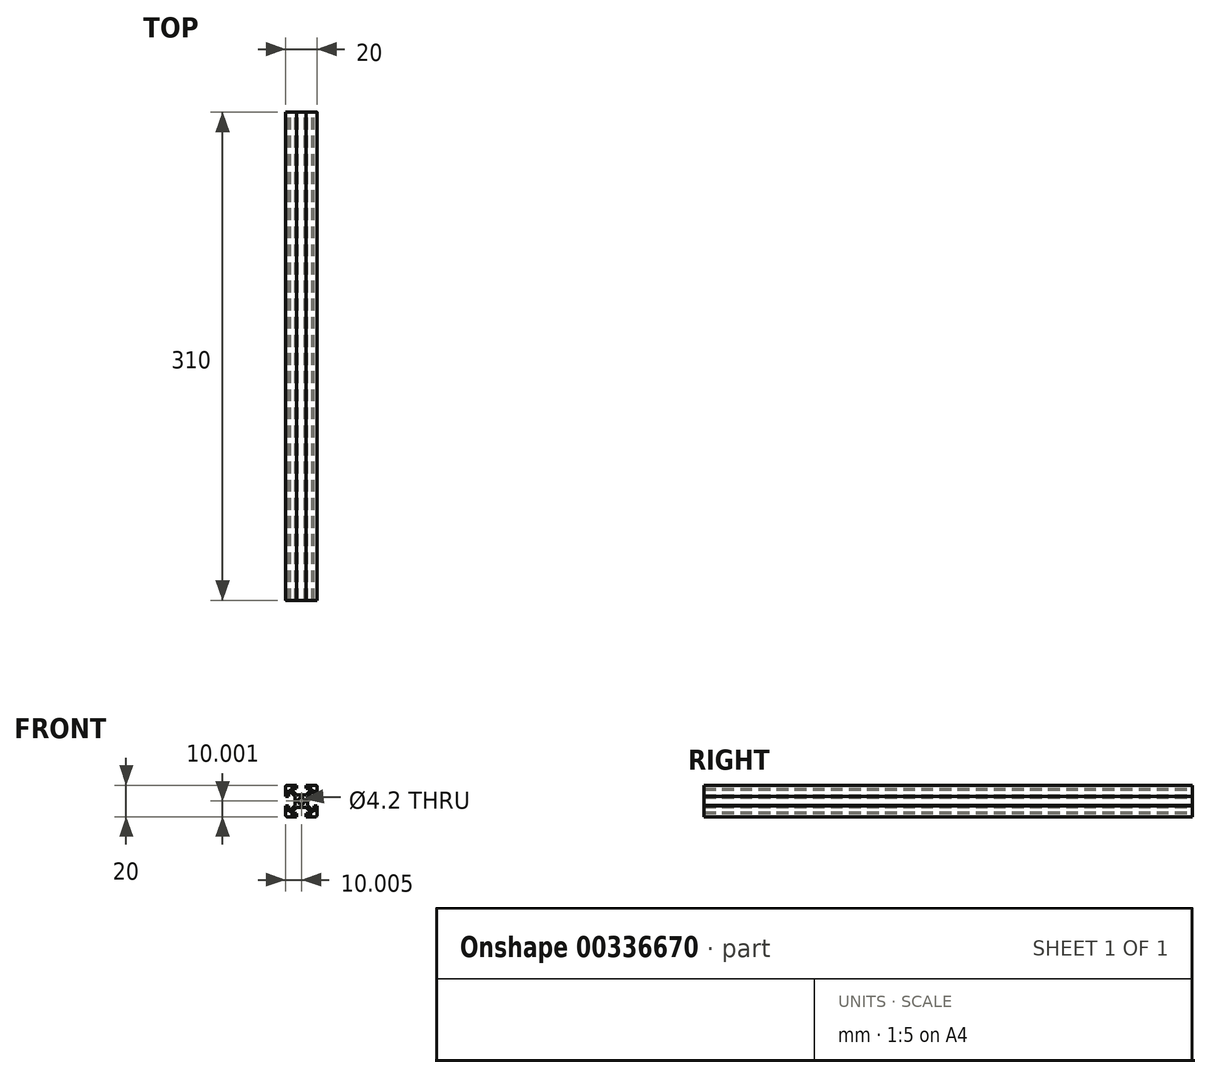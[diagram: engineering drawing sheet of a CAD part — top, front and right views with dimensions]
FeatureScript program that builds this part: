
annotation { "Feature Type Name" : "Feature", "Feature Type Description" : "" }
export const myFeature = defineFeature(function(context is Context, id is Id, definition is map)
    precondition{}
    {
        {
            var Q0;
            Q0=qCreatedBy(makeId("Front.planeOp"),FACE);
            var sketch = newSketch(context, id + "F0", { "sketchPlane" : qUnion([Q0])});
            skCircle(sketch, "E0", {"center": v(-0.06, -0.16) * mm, "radius": 2.1 * mm});
            skLineSegment(sketch, "E1.bottom", {"start": v(8.94, 9.84) * mm, "end": v(2.94, 9.84) * mm});
            skLineSegment(sketch, "E1.top", {"start": v(8.94, -10.16) * mm, "end": v(2.94, -10.16) * mm});
            skLineSegment(sketch, "E1.left", {"start": v(9.94, 8.84) * mm, "end": v(9.94, 2.84) * mm});
            skLineSegment(sketch, "E1.right", {"start": v(-10.06, 8.84) * mm, "end": v(-10.06, 2.84) * mm});
            skLineSegment(sketch, "E2.bottom", {"start": v(2.88, 3.84) * mm, "end": v(-3, 3.84) * mm});
            skLineSegment(sketch, "E2.top", {"start": v(2.88, -4.16) * mm, "end": v(-3, -4.16) * mm});
            skLineSegment(sketch, "E2.left", {"start": v(3.94, 2.78) * mm, "end": v(3.94, -3.1) * mm});
            skLineSegment(sketch, "E2.right", {"start": v(-4.06, 2.78) * mm, "end": v(-4.06, -3.1) * mm});
            skLineSegment(sketch, "E3.bottom", {"start": v(6.88, 7.84) * mm, "end": v(2.94, 7.84) * mm});
            skLineSegment(sketch, "E3.top", {"start": v(6.88, -8.16) * mm, "end": v(2.94, -8.16) * mm});
            skLineSegment(sketch, "E3.left", {"start": v(7.94, 6.78) * mm, "end": v(7.94, 2.84) * mm});
            skLineSegment(sketch, "E3.right", {"start": v(-8.06, 6.78) * mm, "end": v(-8.06, 2.84) * mm});
            skLineSegment(sketch, "E4", {"start": v(-3.06, -10.16) * mm, "end": v(-3.06, -8.16) * mm});
            skLineSegment(sketch, "E5.MirrorCS", {"start": v(2.94, -10.16) * mm, "end": v(2.94, -8.16) * mm});
            skLineSegment(sketch, "E6.MirrorCS", {"start": v(-3.06, 9.84) * mm, "end": v(-3.06, 7.84) * mm});
            skLineSegment(sketch, "E7.MirrorCS", {"start": v(2.94, 9.84) * mm, "end": v(2.94, 7.84) * mm});
            skLineSegment(sketch, "E8", {"start": v(-10.06, 2.84) * mm, "end": v(-8.06, 2.84) * mm});
            skLineSegment(sketch, "E9.MirrorCS", {"start": v(-10.06, -3.16) * mm, "end": v(-8.06, -3.16) * mm});
            skLineSegment(sketch, "E10", {"start": v(7.94, 2.84) * mm, "end": v(9.94, 2.84) * mm});
            skLineSegment(sketch, "E11.MirrorCS", {"start": v(7.94, -3.16) * mm, "end": v(9.94, -3.16) * mm});
            skPoint(sketch, "E12", {"position": v(-8.06, -7.1) * mm});
            skPoint(sketch, "E13", {"position": v(6.88, 7.84) * mm});
            skPoint(sketch, "E14", {"position": v(-4.06, -3.1) * mm});
            skPoint(sketch, "E15", {"position": v(2.88, 3.84) * mm});
            skLineSegment(sketch, "E16", {"start": v(-8.06, -7.1) * mm, "end": v(-4.06, -3.1) * mm});
            skLineSegment(sketch, "E17", {"start": v(2.88, 3.84) * mm, "end": v(6.88, 7.84) * mm});
            skLineSegment(sketch, "E18.MirrorCS", {"start": v(-7, -8.16) * mm, "end": v(-3, -4.16) * mm});
            skLineSegment(sketch, "E19.1.0", {"start": v(6.88, -8.16) * mm, "end": v(2.88, -4.16) * mm});
            skLineSegment(sketch, "E19.2.0", {"start": v(7.94, 6.78) * mm, "end": v(3.94, 2.78) * mm});
            skLineSegment(sketch, "E19.3.0", {"start": v(-7, 7.84) * mm, "end": v(-3, 3.84) * mm});
            skLineSegment(sketch, "E20.1.0", {"start": v(7.94, -7.1) * mm, "end": v(3.94, -3.1) * mm});
            skLineSegment(sketch, "E20.2.0", {"start": v(6.88, 7.84) * mm, "end": v(2.88, 3.84) * mm});
            skLineSegment(sketch, "E20.3.0", {"start": v(-8.06, 6.78) * mm, "end": v(-4.06, 2.78) * mm});
            skLineSegment(sketch, "E21.trimOffspring", {"start": v(-3.06, 7.84) * mm, "end": v(-7, 7.84) * mm});
            skLineSegment(sketch, "E22.trimOffspring", {"start": v(-3.06, 9.84) * mm, "end": v(-9.06, 9.84) * mm});
            skLineSegment(sketch, "E23.trimOffspring", {"start": v(7.94, -3.16) * mm, "end": v(7.94, -7.1) * mm});
            skLineSegment(sketch, "E24.trimOffspring", {"start": v(9.94, -3.16) * mm, "end": v(9.94, -9.16) * mm});
            skLineSegment(sketch, "E25.trimOffspring", {"start": v(-3.06, -10.16) * mm, "end": v(-9.06, -10.16) * mm});
            skLineSegment(sketch, "E26.trimOffspring", {"start": v(-3.06, -8.16) * mm, "end": v(-7, -8.16) * mm});
            skLineSegment(sketch, "E27.trimOffspring", {"start": v(-10.06, -3.16) * mm, "end": v(-10.06, -9.16) * mm});
            skLineSegment(sketch, "E28.trimOffspring", {"start": v(-8.06, -3.16) * mm, "end": v(-8.06, -7.1) * mm});
            skArc(sketch, "E29.filletArc", {"start": v(-10.06, -9.16) * mm, "mid": v(-9.76, -9.87) * mm, "end": v(-9.06, -10.16) * mm});
            skArc(sketch, "E30.filletArc", {"start": v(8.94, -10.16) * mm, "mid": v(9.65, -9.87) * mm, "end": v(9.94, -9.16) * mm});
            skArc(sketch, "E31.filletArc", {"start": v(9.94, 8.84) * mm, "mid": v(9.65, 9.55) * mm, "end": v(8.94, 9.84) * mm});
            skArc(sketch, "E32.filletArc", {"start": v(-9.06, 9.84) * mm, "mid": v(-9.76, 9.55) * mm, "end": v(-10.06, 8.84) * mm});
            skSolve(sketch);
        }
        {
            var Q0;
            Q0=makeQuery(id+"F0.imprint","IMPRINT",FACE,{"disambiguationData":[TD([[makeQuery(id+"F0.imprint","IMPRINT",EDGE,{"derivedFrom":sQuery(id+"F0.wireOp",EDGE,"E0")}),-1.0]])]});
            extrude(context, id + "F1", {"entities" : qUnion([Q0]), "depth" : 310 * mm});
        }
    });
